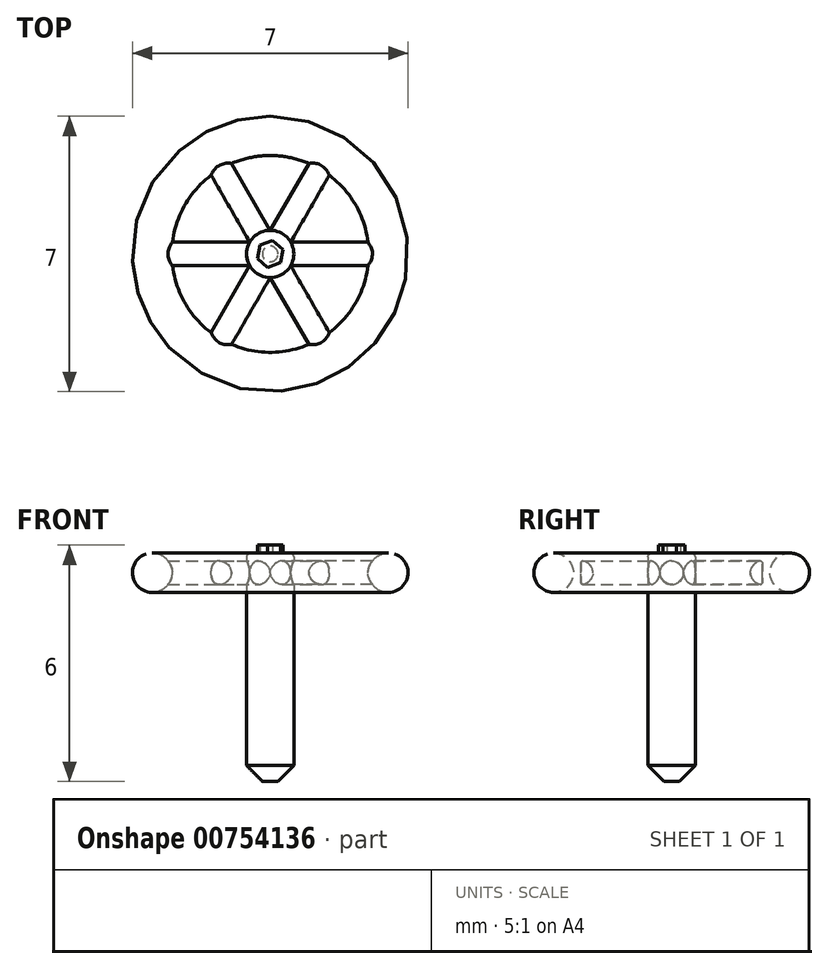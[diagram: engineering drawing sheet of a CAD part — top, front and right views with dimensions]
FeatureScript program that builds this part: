
annotation { "Feature Type Name" : "Feature", "Feature Type Description" : "" }
export const myFeature = defineFeature(function(context is Context, id is Id, definition is map)
    precondition{}
    {
        {
            var Q0;
            Q0=qCreatedBy(makeId("Right.planeOp"),FACE);
            var sketch = newSketch(context, id + "F0", { "sketchPlane" : qUnion([Q0])});
            skLineSegment(sketch, "E0.bottom", {"start": v(0, 0) * mm, "end": v(0.6, 0) * mm});
            skLineSegment(sketch, "E0.top", {"start": v(0, 5.8) * mm, "end": v(0.6, 5.8) * mm});
            skLineSegment(sketch, "E0.left", {"start": v(0, 0) * mm, "end": v(0, 5.8) * mm});
            skLineSegment(sketch, "E0.right", {"start": v(0.6, 0) * mm, "end": v(0.6, 5.8) * mm});
            skCircle(sketch, "E1", {"center": v(3, 5.3) * mm, "radius": 0.5 * mm});
            skPoint(sketch, "E2", {"position": v(3, 5.8) * mm});
            skSolve(sketch);
        }
        {
            var Q0;
            Q0=makeQuery(id+"F0.imprint","IMPRINT",FACE,{"disambiguationData":[TD([[makeQuery(id+"F0.imprint","IMPRINT",EDGE,{"derivedFrom":sQuery(id+"F0.wireOp",EDGE,"E0.bottom")}),1.0]])]});
            var Q1;
            Q1=makeQuery(id+"F0.imprint","IMPRINT",FACE,{"disambiguationData":[TD([[makeQuery(id+"F0.imprint","IMPRINT",EDGE,{"derivedFrom":sQuery(id+"F0.wireOp",EDGE,"E1")}),1.0]])]});
            var Q2;
            Q2=sQuery(id+"F0.wireOp",EDGE,"E0.left");
            revolve(context, id + "F1", {"surfaceOperationType" : NewSurfaceOperationType.NEW, "entities" : qUnion([Q0, Q1]), "axis" : qUnion([Q2]), "revolveType" : RevolveType.FULL});
        }
        {
            var Q0;
            Q0=qCreatedBy(makeId("Right.planeOp"),FACE);
            var sketch = newSketch(context, id + "F2", { "sketchPlane" : qUnion([Q0])});
            skCircle(sketch, "E3", {"center": v(0, 5.3) * mm, "radius": 0.3 * mm});
            skLineSegment(sketch, "E4", {"start": v(0, 5.3) * mm, "end": v(0, 0) * mm, "construction": true});
            skSolve(sketch);
        }
        {
            var Q0;
            Q0 = qSketchRegion(id + "F2", true);
            extrude(context, id + "F3", {"entities" : qUnion([Q0]), "depth" : 2.6 * mm, "offsetDistance" : 25 * mm});
        }
        {
            var Q0;
            Q0=makeQuery(id+"F3.opExtrude","SWEPT_BODY",BODY,{"disambiguationData":[OSD([sQuery(id+"F2.wireOp",EDGE,"E3")])]});
            var Q1;
            Q1=sQuery(id+"F2.wireOp",EDGE,"E4");
            circularPattern(context, id + "F4", {"operationType" : NewBodyOperationType.ADD, "entities" : qUnion([Q0]), "axis" : qUnion([Q1]), "angle" : 360 * degree, "instanceCount" : 6, "equalSpace" : true});
        }
        {
            var Q0;
            Q0=makeQuery(id+"F1.opRevolve","SWEPT_EDGE",EDGE,{"disambiguationData":[OSD([sQuery(id+"F0.wireOp",EDGE,"E0.top"),sQuery(id+"F0.wireOp",EDGE,"E0.right")])]});
            fillet(context, id + "F5", {"entities" : qUnion([Q0]), "radius" : 0.1 * mm, "tangentPropagation" : true, "allowEdgeOverflow" : false});
        }
        {
            var Q0;
            Q0=makeQuery(id+"F1.opRevolve","SWEPT_FACE",FACE,{"disambiguationData":[OSD([sQuery(id+"F0.wireOp",EDGE,"E0.top")])]});
            var sketch = newSketch(context, id + "F6", { "sketchPlane" : qUnion([Q0])});
            skCircle(sketch, "E5.cCircle", {"center": v(0, 0) * mm, "radius": 0.3 * mm, "construction": true});
            skLineSegment(sketch, "E5.0", {"start": v(0.06, 0.34) * mm, "end": v(0.33, 0.12) * mm});
            skLineSegment(sketch, "E5.1", {"start": v(0.33, 0.12) * mm, "end": v(0.26, -0.22) * mm});
            skLineSegment(sketch, "E5.2", {"start": v(0.26, -0.22) * mm, "end": v(-0.06, -0.34) * mm});
            skLineSegment(sketch, "E5.3", {"start": v(-0.06, -0.34) * mm, "end": v(-0.33, -0.12) * mm});
            skLineSegment(sketch, "E5.4", {"start": v(-0.33, -0.12) * mm, "end": v(-0.26, 0.22) * mm});
            skLineSegment(sketch, "E5.5", {"start": v(-0.26, 0.22) * mm, "end": v(0.06, 0.34) * mm});
            skPoint(sketch, "E5.0.midPoint", {"position": v(0.2, 0.23) * mm});
            skSolve(sketch);
        }
        {
            var Q0;
            Q0 = qSketchRegion(id + "F6", true);
            extrude(context, id + "F7", {"entities" : qUnion([Q0]), "operationType" : NewBodyOperationType.ADD, "depth" : 0.2 * mm, "offsetDistance" : 25 * mm});
        }
        {
            var Q0;
            Q0=makeQuery(id+"F1.opRevolve","SWEPT_EDGE",EDGE,{"disambiguationData":[OSD([sQuery(id+"F0.wireOp",EDGE,"E0.bottom"),sQuery(id+"F0.wireOp",EDGE,"E0.right")])]});
            chamfer(context, id + "F8", {"entities" : qUnion([Q0]), "width" : 0.4 * mm, "tangentPropagation" : true});
        }
    });
